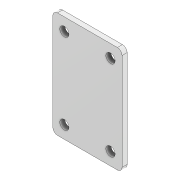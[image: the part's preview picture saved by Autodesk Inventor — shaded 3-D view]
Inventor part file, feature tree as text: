
AUTODESK INVENTOR PART (.ipt)
format: ipt  version: 2020 (Build 240168000, 168)  size: 103,936 bytes
history: native  units: mm
features: other x1, extrude x1, fillet x1, sketch x1
ambient origin geometry x8: Origin, YZ Plane, XZ Plane, XY Plane, X Axis, Y Axis, Z Axis, Center Point
bodies: Body1 (feature_tree)
feature tree (4):
  other  "솔리드1"
  extrude  "돌출1"  Depth=30.0mm
  fillet  "모깎기1"  Radius=46.0mm
  sketch  "스케치1"
